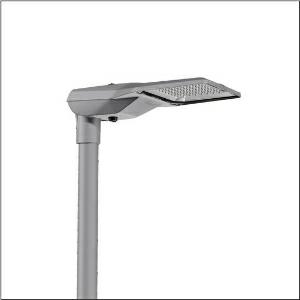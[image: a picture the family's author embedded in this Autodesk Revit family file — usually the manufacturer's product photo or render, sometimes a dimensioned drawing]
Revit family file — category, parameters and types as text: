
# Revit family: streetlight_sl_21_midi___st0_8a_5xe3c33t08mb_c889
name_source: partatom
category: Lighting Fixtures
units: mm (PartAtom-declared; Revit-internal decimal feet)

## family parameters
Cut with Voids When Loaded = No
Host = Face
Light Source = No
Part Type = Normal
Room Calculation Point = No
Round Connector Dimension = Use Diameter
Shared = No

## types (1)
- --- (1 x LED, 18270 lm, 136 W, 3000K)
    Apparent Load = 136 VA
    CIE Flux Codes = 38 75 97 100 100
    Color Rendering = 70
    Color Temperature = 3000K
    Default Elevation = 1800 mm
    Description = Streetlight SL 21 midi, mast luminaire, primary light control with lens, of PMMA, primary optical cover: cover, of toughened safety glass, transparent, light distribution: ST0.8a, light emission: direct distribution, primary light characteristic: asymmetric, installation type: side-entry, post-top, LED, High Power LED, rated luminous flux: 18.270lm, luminous efficacy: 134lm/W, light colour: 730, colour temperature: 3000K, control gear: D4i, control: overheat protection, constant luminous flux control, time-dependent luminous flux control, flexible luminous flux parameterisation, pre-setting: logarithmic dimming characteristic, mains connection: 230..240V, AC, 50/60Hz, start of lifetime: 136W, end of service life: 142W, reduction: 61W, luminaire housing, of diecast aluminium, powder-coated, SITECO metallic grey (DB 702S), corrosivity category C5 high according to DIN EN ISO 12944, please order mast flange separately, inclination adjustable: 0°, 5°, 10°, 15°, sealing non-destructively replaceable, multi-level sealing system, length: 644mm, width: 335mm, height: 110mm, mast flange for spigot size: 42mm (side-entry): 5XC10008XM4, 60/48mm (side-entry/post-top): 5XC10108XM2, 76/60mm (side-entry/post-top): 5XC10108XM1, mounting height: 4..8m, Smart Interface below and above, protection rating (complete): IP66, insulation class (complete): insulation class II (safety insulation), certification: CE, ENEC, ENEC+, VDE, impact resistance: IK10, permissible operating ambient temperature for outdoor applications: -40..+50°C, standard-compliant lighting for roads and squares, packaging unit: 1 piece

Light Distribution: ST0.8a
    Height = 111 mm
    Lamp = 1 x LED
    Lamp Light Flux = 18270 lm
    Lamp Power = 136 W
    Lamp count = 1
    Length = 644 mm
    Luminous efficacy = 134 lm/W
    Manufacturer = Siteco
    ModVariant = No
    Model = 5XE3C33T08MB
    Number of Poles = 1
    OnlyDefault = Yes
    Power Factor = 1
    Product Name = Streetlight SL 21 midi | ST0.8a
    Product group = mast luminaire | pylon top
    ProductGroupID = 6100
    Protection Class = Protection class II
    Protection Degree = IP 66
    RLX_Detail_Level = 1
    RLX_Emergency_Light_Flux = 0 lm
    RLX_Emergency_Type = 0
    RLX_Emergency_Type_DB = No
    RlxData = <blob elided: 27061 chars, md5=3631e50b>
    Socket = socket
    Standby Power = 0 W
    System Light Flux = 18270 lm
    System Power = 136 W
    Type Comments = factory setting: luminous flux: 100 % | dim-lin: 254 | 695 mA
    Type Image = l_1004304.jpg
    URL = http://relux.com
    VarID = @adj_183493
    Voltage = 0 V
    Weight = 0.00 kg
    Width = 336 mm

## geometry (parser evidence)
native form markers: Blend x4, Sweep x12
no freeform markers — native parametric forms only
